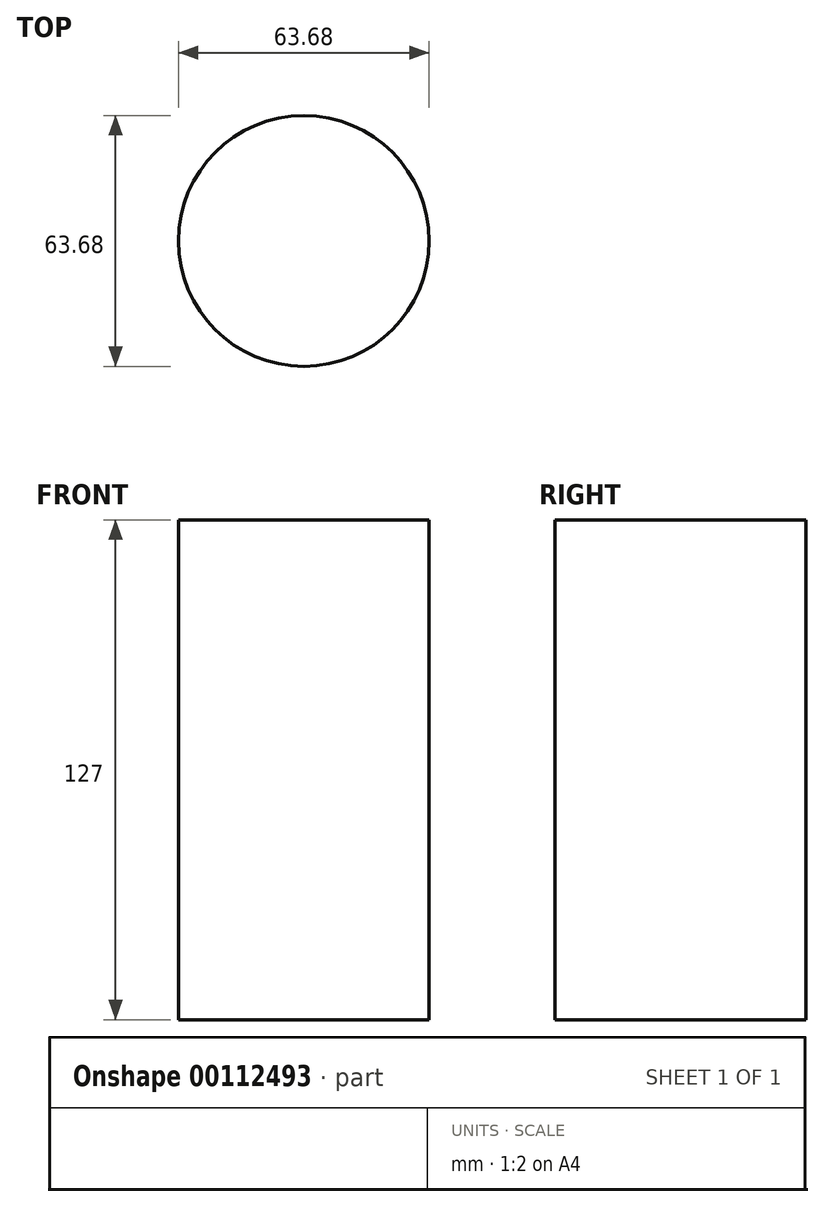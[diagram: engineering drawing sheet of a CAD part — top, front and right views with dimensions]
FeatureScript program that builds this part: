
annotation { "Feature Type Name" : "Feature", "Feature Type Description" : "" }
export const myFeature = defineFeature(function(context is Context, id is Id, definition is map)
    precondition{}
    {
        {
            var Q0;
            Q0=qCreatedBy(makeId("Top.planeOp"),FACE);
            var sketch = newSketch(context, id + "F0", { "sketchPlane" : qUnion([Q0])});
            skCircle(sketch, "E0", {"center": v(0, 0) * mm, "radius": 31.84 * mm});
            skSolve(sketch);
        }
        {
            var Q0;
            Q0=makeQuery(id+"F0.imprint","IMPRINT",FACE,{"disambiguationData":[TD([[makeQuery(id+"F0.imprint","IMPRINT",EDGE,{"derivedFrom":sQuery(id+"F0.wireOp",EDGE,"E0")}),1.0]])]});
            extrude(context, id + "F1", {"entities" : qUnion([Q0]), "depth" : 127 * mm});
        }
    });
